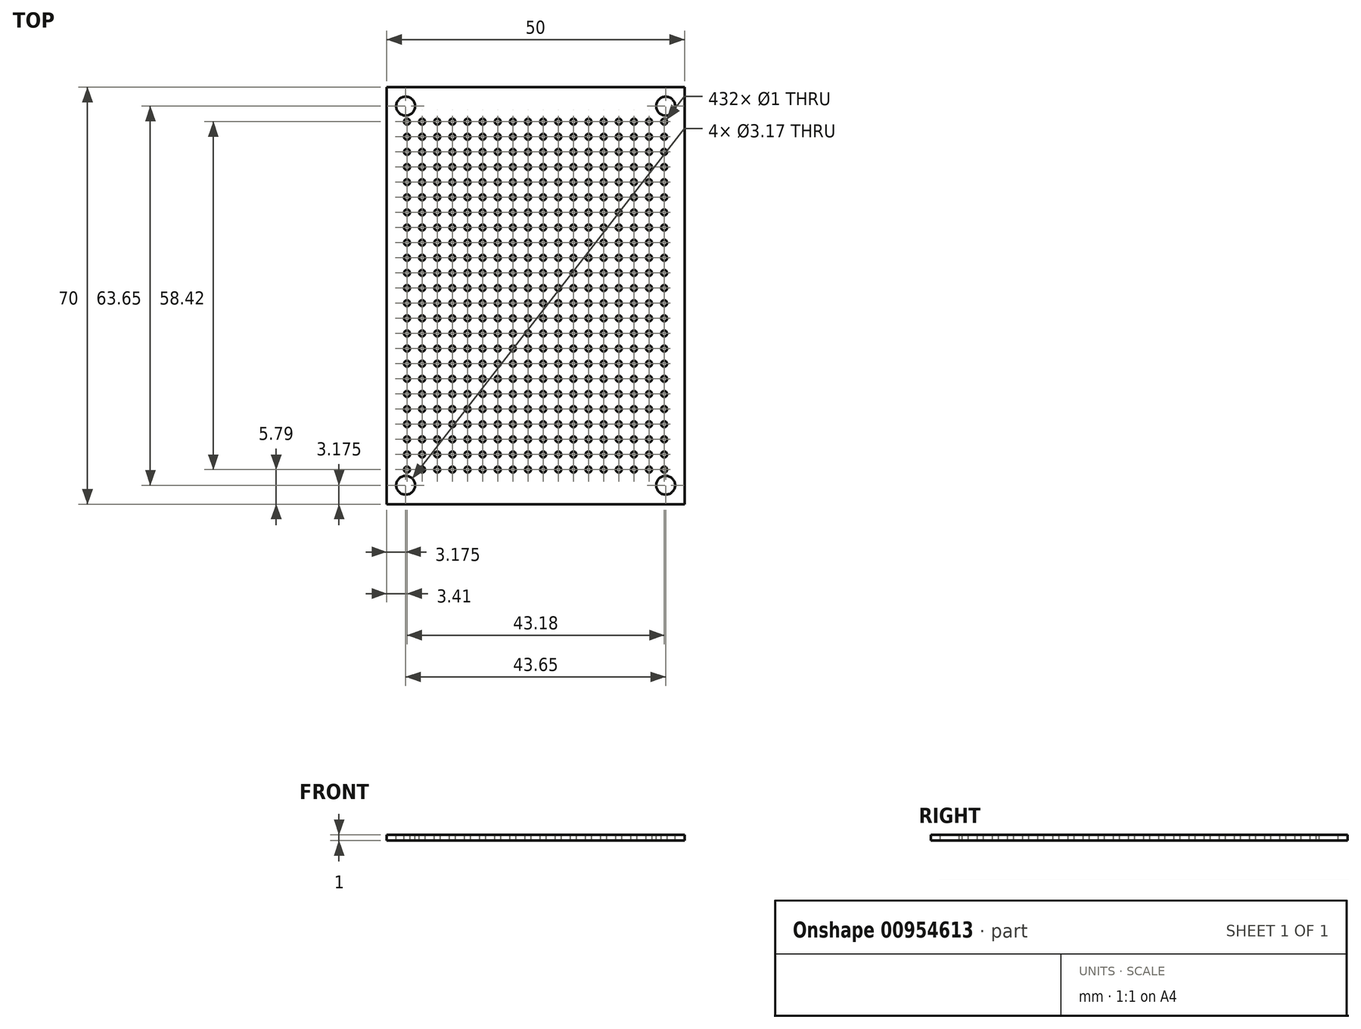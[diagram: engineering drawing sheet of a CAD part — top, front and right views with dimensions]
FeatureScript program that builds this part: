
annotation { "Feature Type Name" : "Feature", "Feature Type Description" : "" }
export const myFeature = defineFeature(function(context is Context, id is Id, definition is map)
    precondition{}
    {
        {
            var Q0;
            Q0=qCreatedBy(makeId("Top.planeOp"),FACE);
            var sketch = newSketch(context, id + "F0", { "sketchPlane" : qUnion([Q0])});
            skLineSegment(sketch, "E0.bottom", {"start": v(-25, 35) * mm, "end": v(25, 35) * mm});
            skLineSegment(sketch, "E0.top", {"start": v(-25, -35) * mm, "end": v(25, -35) * mm});
            skLineSegment(sketch, "E0.left", {"start": v(-25, 35) * mm, "end": v(-25, -35) * mm});
            skLineSegment(sketch, "E0.right", {"start": v(25, 35) * mm, "end": v(25, -35) * mm});
            skPoint(sketch, "E0.middle", {"position": v(0, 0) * mm});
            skSolve(sketch);
        }
        {
            var Q0;
            Q0=qSketchRegion(id+"F0",true);
            extrude(context, id + "F1", {"entities" : qUnion([Q0]), "depth" : 1 * mm, "offsetDistance" : 25 * mm});
        }
        {
            var Q0;
            Q0=makeQuery(id+"F1.opExtrude","CAP_FACE",FACE,{"disambiguationData":[OSD([sQuery(id+"F0.wireOp",EDGE,"E0.bottom"),sQuery(id+"F0.wireOp",EDGE,"E0.top"),sQuery(id+"F0.wireOp",EDGE,"E0.left"),sQuery(id+"F0.wireOp",EDGE,"E0.right")])],"isStart":false});
            var sketch = newSketch(context, id + "F2", { "sketchPlane" : qUnion([Q0])});
            skCircle(sketch, "E1", {"center": v(-21.59, 29.21) * mm, "radius": 0.5 * mm});
            skCircle(sketch, "E2.0.1.0", {"center": v(-21.59, 26.67) * mm, "radius": 0.5 * mm});
            skCircle(sketch, "E2.0.2.0", {"center": v(-21.59, 24.13) * mm, "radius": 0.5 * mm});
            skCircle(sketch, "E2.0.3.0", {"center": v(-21.59, 21.6) * mm, "radius": 0.5 * mm});
            skCircle(sketch, "E2.0.4.0", {"center": v(-21.59, 19.05) * mm, "radius": 0.5 * mm});
            skCircle(sketch, "E2.0.5.0", {"center": v(-21.59, 16.51) * mm, "radius": 0.5 * mm});
            skCircle(sketch, "E2.0.6.0", {"center": v(-21.59, 13.97) * mm, "radius": 0.5 * mm});
            skCircle(sketch, "E2.0.7.0", {"center": v(-21.59, 11.43) * mm, "radius": 0.5 * mm});
            skCircle(sketch, "E2.0.8.0", {"center": v(-21.59, 8.9) * mm, "radius": 0.5 * mm});
            skCircle(sketch, "E2.0.9.0", {"center": v(-21.59, 6.35) * mm, "radius": 0.5 * mm});
            skCircle(sketch, "E2.0.10.0", {"center": v(-21.59, 3.81) * mm, "radius": 0.5 * mm});
            skCircle(sketch, "E2.0.11.0", {"center": v(-21.59, 1.27) * mm, "radius": 0.5 * mm});
            skCircle(sketch, "E2.0.12.0", {"center": v(-21.59, -1.27) * mm, "radius": 0.5 * mm});
            skCircle(sketch, "E2.0.13.0", {"center": v(-21.59, -3.8) * mm, "radius": 0.5 * mm});
            skCircle(sketch, "E2.0.14.0", {"center": v(-21.59, -6.35) * mm, "radius": 0.5 * mm});
            skCircle(sketch, "E2.0.15.0", {"center": v(-21.59, -8.89) * mm, "radius": 0.5 * mm});
            skCircle(sketch, "E2.0.16.0", {"center": v(-21.59, -11.43) * mm, "radius": 0.5 * mm});
            skCircle(sketch, "E2.0.17.0", {"center": v(-21.59, -13.97) * mm, "radius": 0.5 * mm});
            skCircle(sketch, "E2.0.18.0", {"center": v(-21.59, -16.5) * mm, "radius": 0.5 * mm});
            skCircle(sketch, "E2.0.19.0", {"center": v(-21.59, -19.05) * mm, "radius": 0.5 * mm});
            skCircle(sketch, "E2.0.20.0", {"center": v(-21.59, -21.59) * mm, "radius": 0.5 * mm});
            skCircle(sketch, "E2.0.21.0", {"center": v(-21.59, -24.13) * mm, "radius": 0.5 * mm});
            skCircle(sketch, "E2.0.22.0", {"center": v(-21.59, -26.67) * mm, "radius": 0.5 * mm});
            skCircle(sketch, "E2.0.23.0", {"center": v(-21.59, -29.2) * mm, "radius": 0.5 * mm});
            skCircle(sketch, "E2.1.0.0", {"center": v(-19.05, 29.21) * mm, "radius": 0.5 * mm});
            skCircle(sketch, "E2.1.1.0", {"center": v(-19.05, 26.67) * mm, "radius": 0.5 * mm});
            skCircle(sketch, "E2.1.2.0", {"center": v(-19.05, 24.13) * mm, "radius": 0.5 * mm});
            skCircle(sketch, "E2.1.3.0", {"center": v(-19.05, 21.6) * mm, "radius": 0.5 * mm});
            skCircle(sketch, "E2.1.4.0", {"center": v(-19.05, 19.05) * mm, "radius": 0.5 * mm});
            skCircle(sketch, "E2.1.5.0", {"center": v(-19.05, 16.51) * mm, "radius": 0.5 * mm});
            skCircle(sketch, "E2.1.6.0", {"center": v(-19.05, 13.97) * mm, "radius": 0.5 * mm});
            skCircle(sketch, "E2.1.7.0", {"center": v(-19.05, 11.43) * mm, "radius": 0.5 * mm});
            skCircle(sketch, "E2.1.8.0", {"center": v(-19.05, 8.9) * mm, "radius": 0.5 * mm});
            skCircle(sketch, "E2.1.9.0", {"center": v(-19.05, 6.35) * mm, "radius": 0.5 * mm});
            skCircle(sketch, "E2.1.10.0", {"center": v(-19.05, 3.81) * mm, "radius": 0.5 * mm});
            skCircle(sketch, "E2.1.11.0", {"center": v(-19.05, 1.27) * mm, "radius": 0.5 * mm});
            skCircle(sketch, "E2.1.12.0", {"center": v(-19.05, -1.27) * mm, "radius": 0.5 * mm});
            skCircle(sketch, "E2.1.13.0", {"center": v(-19.05, -3.8) * mm, "radius": 0.5 * mm});
            skCircle(sketch, "E2.1.14.0", {"center": v(-19.05, -6.35) * mm, "radius": 0.5 * mm});
            skCircle(sketch, "E2.1.15.0", {"center": v(-19.05, -8.89) * mm, "radius": 0.5 * mm});
            skCircle(sketch, "E2.1.16.0", {"center": v(-19.05, -11.43) * mm, "radius": 0.5 * mm});
            skCircle(sketch, "E2.1.17.0", {"center": v(-19.05, -13.97) * mm, "radius": 0.5 * mm});
            skCircle(sketch, "E2.1.18.0", {"center": v(-19.05, -16.5) * mm, "radius": 0.5 * mm});
            skCircle(sketch, "E2.1.19.0", {"center": v(-19.05, -19.05) * mm, "radius": 0.5 * mm});
            skCircle(sketch, "E2.1.20.0", {"center": v(-19.05, -21.59) * mm, "radius": 0.5 * mm});
            skCircle(sketch, "E2.1.21.0", {"center": v(-19.05, -24.13) * mm, "radius": 0.5 * mm});
            skCircle(sketch, "E2.1.22.0", {"center": v(-19.05, -26.67) * mm, "radius": 0.5 * mm});
            skCircle(sketch, "E2.1.23.0", {"center": v(-19.05, -29.2) * mm, "radius": 0.5 * mm});
            skCircle(sketch, "E2.2.0.0", {"center": v(-16.5, 29.21) * mm, "radius": 0.5 * mm});
            skCircle(sketch, "E2.2.1.0", {"center": v(-16.5, 26.67) * mm, "radius": 0.5 * mm});
            skCircle(sketch, "E2.2.2.0", {"center": v(-16.5, 24.13) * mm, "radius": 0.5 * mm});
            skCircle(sketch, "E2.2.3.0", {"center": v(-16.5, 21.6) * mm, "radius": 0.5 * mm});
            skCircle(sketch, "E2.2.4.0", {"center": v(-16.5, 19.05) * mm, "radius": 0.5 * mm});
            skCircle(sketch, "E2.2.5.0", {"center": v(-16.5, 16.51) * mm, "radius": 0.5 * mm});
            skCircle(sketch, "E2.2.6.0", {"center": v(-16.5, 13.97) * mm, "radius": 0.5 * mm});
            skCircle(sketch, "E2.2.7.0", {"center": v(-16.5, 11.43) * mm, "radius": 0.5 * mm});
            skCircle(sketch, "E2.2.8.0", {"center": v(-16.5, 8.9) * mm, "radius": 0.5 * mm});
            skCircle(sketch, "E2.2.9.0", {"center": v(-16.5, 6.35) * mm, "radius": 0.5 * mm});
            skCircle(sketch, "E2.2.10.0", {"center": v(-16.5, 3.81) * mm, "radius": 0.5 * mm});
            skCircle(sketch, "E2.2.11.0", {"center": v(-16.5, 1.27) * mm, "radius": 0.5 * mm});
            skCircle(sketch, "E2.2.12.0", {"center": v(-16.5, -1.27) * mm, "radius": 0.5 * mm});
            skCircle(sketch, "E2.2.13.0", {"center": v(-16.5, -3.8) * mm, "radius": 0.5 * mm});
            skCircle(sketch, "E2.2.14.0", {"center": v(-16.5, -6.35) * mm, "radius": 0.5 * mm});
            skCircle(sketch, "E2.2.15.0", {"center": v(-16.5, -8.89) * mm, "radius": 0.5 * mm});
            skCircle(sketch, "E2.2.16.0", {"center": v(-16.5, -11.43) * mm, "radius": 0.5 * mm});
            skCircle(sketch, "E2.2.17.0", {"center": v(-16.5, -13.97) * mm, "radius": 0.5 * mm});
            skCircle(sketch, "E2.2.18.0", {"center": v(-16.5, -16.5) * mm, "radius": 0.5 * mm});
            skCircle(sketch, "E2.2.19.0", {"center": v(-16.5, -19.05) * mm, "radius": 0.5 * mm});
            skCircle(sketch, "E2.2.20.0", {"center": v(-16.5, -21.59) * mm, "radius": 0.5 * mm});
            skCircle(sketch, "E2.2.21.0", {"center": v(-16.5, -24.13) * mm, "radius": 0.5 * mm});
            skCircle(sketch, "E2.2.22.0", {"center": v(-16.5, -26.67) * mm, "radius": 0.5 * mm});
            skCircle(sketch, "E2.2.23.0", {"center": v(-16.5, -29.2) * mm, "radius": 0.5 * mm});
            skCircle(sketch, "E2.3.0.0", {"center": v(-13.97, 29.21) * mm, "radius": 0.5 * mm});
            skCircle(sketch, "E2.3.1.0", {"center": v(-13.97, 26.67) * mm, "radius": 0.5 * mm});
            skCircle(sketch, "E2.3.2.0", {"center": v(-13.97, 24.13) * mm, "radius": 0.5 * mm});
            skCircle(sketch, "E2.3.3.0", {"center": v(-13.97, 21.6) * mm, "radius": 0.5 * mm});
            skCircle(sketch, "E2.3.4.0", {"center": v(-13.97, 19.05) * mm, "radius": 0.5 * mm});
            skCircle(sketch, "E2.3.5.0", {"center": v(-13.97, 16.51) * mm, "radius": 0.5 * mm});
            skCircle(sketch, "E2.3.6.0", {"center": v(-13.97, 13.97) * mm, "radius": 0.5 * mm});
            skCircle(sketch, "E2.3.7.0", {"center": v(-13.97, 11.43) * mm, "radius": 0.5 * mm});
            skCircle(sketch, "E2.3.8.0", {"center": v(-13.97, 8.9) * mm, "radius": 0.5 * mm});
            skCircle(sketch, "E2.3.9.0", {"center": v(-13.97, 6.35) * mm, "radius": 0.5 * mm});
            skCircle(sketch, "E2.3.10.0", {"center": v(-13.97, 3.81) * mm, "radius": 0.5 * mm});
            skCircle(sketch, "E2.3.11.0", {"center": v(-13.97, 1.27) * mm, "radius": 0.5 * mm});
            skCircle(sketch, "E2.3.12.0", {"center": v(-13.97, -1.27) * mm, "radius": 0.5 * mm});
            skCircle(sketch, "E2.3.13.0", {"center": v(-13.97, -3.8) * mm, "radius": 0.5 * mm});
            skCircle(sketch, "E2.3.14.0", {"center": v(-13.97, -6.35) * mm, "radius": 0.5 * mm});
            skCircle(sketch, "E2.3.15.0", {"center": v(-13.97, -8.89) * mm, "radius": 0.5 * mm});
            skCircle(sketch, "E2.3.16.0", {"center": v(-13.97, -11.43) * mm, "radius": 0.5 * mm});
            skCircle(sketch, "E2.3.17.0", {"center": v(-13.97, -13.97) * mm, "radius": 0.5 * mm});
            skCircle(sketch, "E2.3.18.0", {"center": v(-13.97, -16.5) * mm, "radius": 0.5 * mm});
            skCircle(sketch, "E2.3.19.0", {"center": v(-13.97, -19.05) * mm, "radius": 0.5 * mm});
            skCircle(sketch, "E2.3.20.0", {"center": v(-13.97, -21.59) * mm, "radius": 0.5 * mm});
            skCircle(sketch, "E2.3.21.0", {"center": v(-13.97, -24.13) * mm, "radius": 0.5 * mm});
            skCircle(sketch, "E2.3.22.0", {"center": v(-13.97, -26.67) * mm, "radius": 0.5 * mm});
            skCircle(sketch, "E2.3.23.0", {"center": v(-13.97, -29.2) * mm, "radius": 0.5 * mm});
            skCircle(sketch, "E2.4.0.0", {"center": v(-11.43, 29.21) * mm, "radius": 0.5 * mm});
            skCircle(sketch, "E2.4.1.0", {"center": v(-11.43, 26.67) * mm, "radius": 0.5 * mm});
            skCircle(sketch, "E2.4.2.0", {"center": v(-11.43, 24.13) * mm, "radius": 0.5 * mm});
            skCircle(sketch, "E2.4.3.0", {"center": v(-11.43, 21.6) * mm, "radius": 0.5 * mm});
            skCircle(sketch, "E2.4.4.0", {"center": v(-11.43, 19.05) * mm, "radius": 0.5 * mm});
            skCircle(sketch, "E2.4.5.0", {"center": v(-11.43, 16.51) * mm, "radius": 0.5 * mm});
            skCircle(sketch, "E2.4.6.0", {"center": v(-11.43, 13.97) * mm, "radius": 0.5 * mm});
            skCircle(sketch, "E2.4.7.0", {"center": v(-11.43, 11.43) * mm, "radius": 0.5 * mm});
            skCircle(sketch, "E2.4.8.0", {"center": v(-11.43, 8.9) * mm, "radius": 0.5 * mm});
            skCircle(sketch, "E2.4.9.0", {"center": v(-11.43, 6.35) * mm, "radius": 0.5 * mm});
            skCircle(sketch, "E2.4.10.0", {"center": v(-11.43, 3.81) * mm, "radius": 0.5 * mm});
            skCircle(sketch, "E2.4.11.0", {"center": v(-11.43, 1.27) * mm, "radius": 0.5 * mm});
            skCircle(sketch, "E2.4.12.0", {"center": v(-11.43, -1.27) * mm, "radius": 0.5 * mm});
            skCircle(sketch, "E2.4.13.0", {"center": v(-11.43, -3.8) * mm, "radius": 0.5 * mm});
            skCircle(sketch, "E2.4.14.0", {"center": v(-11.43, -6.35) * mm, "radius": 0.5 * mm});
            skCircle(sketch, "E2.4.15.0", {"center": v(-11.43, -8.89) * mm, "radius": 0.5 * mm});
            skCircle(sketch, "E2.4.16.0", {"center": v(-11.43, -11.43) * mm, "radius": 0.5 * mm});
            skCircle(sketch, "E2.4.17.0", {"center": v(-11.43, -13.97) * mm, "radius": 0.5 * mm});
            skCircle(sketch, "E2.4.18.0", {"center": v(-11.43, -16.5) * mm, "radius": 0.5 * mm});
            skCircle(sketch, "E2.4.19.0", {"center": v(-11.43, -19.05) * mm, "radius": 0.5 * mm});
            skCircle(sketch, "E2.4.20.0", {"center": v(-11.43, -21.59) * mm, "radius": 0.5 * mm});
            skCircle(sketch, "E2.4.21.0", {"center": v(-11.43, -24.13) * mm, "radius": 0.5 * mm});
            skCircle(sketch, "E2.4.22.0", {"center": v(-11.43, -26.67) * mm, "radius": 0.5 * mm});
            skCircle(sketch, "E2.4.23.0", {"center": v(-11.43, -29.2) * mm, "radius": 0.5 * mm});
            skCircle(sketch, "E2.5.0.0", {"center": v(-8.89, 29.21) * mm, "radius": 0.5 * mm});
            skCircle(sketch, "E2.5.1.0", {"center": v(-8.89, 26.67) * mm, "radius": 0.5 * mm});
            skCircle(sketch, "E2.5.2.0", {"center": v(-8.89, 24.13) * mm, "radius": 0.5 * mm});
            skCircle(sketch, "E2.5.3.0", {"center": v(-8.89, 21.6) * mm, "radius": 0.5 * mm});
            skCircle(sketch, "E2.5.4.0", {"center": v(-8.89, 19.05) * mm, "radius": 0.5 * mm});
            skCircle(sketch, "E2.5.5.0", {"center": v(-8.89, 16.51) * mm, "radius": 0.5 * mm});
            skCircle(sketch, "E2.5.6.0", {"center": v(-8.89, 13.97) * mm, "radius": 0.5 * mm});
            skCircle(sketch, "E2.5.7.0", {"center": v(-8.89, 11.43) * mm, "radius": 0.5 * mm});
            skCircle(sketch, "E2.5.8.0", {"center": v(-8.89, 8.9) * mm, "radius": 0.5 * mm});
            skCircle(sketch, "E2.5.9.0", {"center": v(-8.89, 6.35) * mm, "radius": 0.5 * mm});
            skCircle(sketch, "E2.5.10.0", {"center": v(-8.89, 3.81) * mm, "radius": 0.5 * mm});
            skCircle(sketch, "E2.5.11.0", {"center": v(-8.89, 1.27) * mm, "radius": 0.5 * mm});
            skCircle(sketch, "E2.5.12.0", {"center": v(-8.89, -1.27) * mm, "radius": 0.5 * mm});
            skCircle(sketch, "E2.5.13.0", {"center": v(-8.89, -3.8) * mm, "radius": 0.5 * mm});
            skCircle(sketch, "E2.5.14.0", {"center": v(-8.89, -6.35) * mm, "radius": 0.5 * mm});
            skCircle(sketch, "E2.5.15.0", {"center": v(-8.89, -8.89) * mm, "radius": 0.5 * mm});
            skCircle(sketch, "E2.5.16.0", {"center": v(-8.89, -11.43) * mm, "radius": 0.5 * mm});
            skCircle(sketch, "E2.5.17.0", {"center": v(-8.89, -13.97) * mm, "radius": 0.5 * mm});
            skCircle(sketch, "E2.5.18.0", {"center": v(-8.89, -16.5) * mm, "radius": 0.5 * mm});
            skCircle(sketch, "E2.5.19.0", {"center": v(-8.89, -19.05) * mm, "radius": 0.5 * mm});
            skCircle(sketch, "E2.5.20.0", {"center": v(-8.89, -21.59) * mm, "radius": 0.5 * mm});
            skCircle(sketch, "E2.5.21.0", {"center": v(-8.89, -24.13) * mm, "radius": 0.5 * mm});
            skCircle(sketch, "E2.5.22.0", {"center": v(-8.89, -26.67) * mm, "radius": 0.5 * mm});
            skCircle(sketch, "E2.5.23.0", {"center": v(-8.89, -29.2) * mm, "radius": 0.5 * mm});
            skCircle(sketch, "E2.6.0.0", {"center": v(-6.35, 29.21) * mm, "radius": 0.5 * mm});
            skCircle(sketch, "E2.6.1.0", {"center": v(-6.35, 26.67) * mm, "radius": 0.5 * mm});
            skCircle(sketch, "E2.6.2.0", {"center": v(-6.35, 24.13) * mm, "radius": 0.5 * mm});
            skCircle(sketch, "E2.6.3.0", {"center": v(-6.35, 21.6) * mm, "radius": 0.5 * mm});
            skCircle(sketch, "E2.6.4.0", {"center": v(-6.35, 19.05) * mm, "radius": 0.5 * mm});
            skCircle(sketch, "E2.6.5.0", {"center": v(-6.35, 16.51) * mm, "radius": 0.5 * mm});
            skCircle(sketch, "E2.6.6.0", {"center": v(-6.35, 13.97) * mm, "radius": 0.5 * mm});
            skCircle(sketch, "E2.6.7.0", {"center": v(-6.35, 11.43) * mm, "radius": 0.5 * mm});
            skCircle(sketch, "E2.6.8.0", {"center": v(-6.35, 8.9) * mm, "radius": 0.5 * mm});
            skCircle(sketch, "E2.6.9.0", {"center": v(-6.35, 6.35) * mm, "radius": 0.5 * mm});
            skCircle(sketch, "E2.6.10.0", {"center": v(-6.35, 3.81) * mm, "radius": 0.5 * mm});
            skCircle(sketch, "E2.6.11.0", {"center": v(-6.35, 1.27) * mm, "radius": 0.5 * mm});
            skCircle(sketch, "E2.6.12.0", {"center": v(-6.35, -1.27) * mm, "radius": 0.5 * mm});
            skCircle(sketch, "E2.6.13.0", {"center": v(-6.35, -3.8) * mm, "radius": 0.5 * mm});
            skCircle(sketch, "E2.6.14.0", {"center": v(-6.35, -6.35) * mm, "radius": 0.5 * mm});
            skCircle(sketch, "E2.6.15.0", {"center": v(-6.35, -8.89) * mm, "radius": 0.5 * mm});
            skCircle(sketch, "E2.6.16.0", {"center": v(-6.35, -11.43) * mm, "radius": 0.5 * mm});
            skCircle(sketch, "E2.6.17.0", {"center": v(-6.35, -13.97) * mm, "radius": 0.5 * mm});
            skCircle(sketch, "E2.6.18.0", {"center": v(-6.35, -16.5) * mm, "radius": 0.5 * mm});
            skCircle(sketch, "E2.6.19.0", {"center": v(-6.35, -19.05) * mm, "radius": 0.5 * mm});
            skCircle(sketch, "E2.6.20.0", {"center": v(-6.35, -21.59) * mm, "radius": 0.5 * mm});
            skCircle(sketch, "E2.6.21.0", {"center": v(-6.35, -24.13) * mm, "radius": 0.5 * mm});
            skCircle(sketch, "E2.6.22.0", {"center": v(-6.35, -26.67) * mm, "radius": 0.5 * mm});
            skCircle(sketch, "E2.6.23.0", {"center": v(-6.35, -29.2) * mm, "radius": 0.5 * mm});
            skCircle(sketch, "E2.7.0.0", {"center": v(-3.8, 29.21) * mm, "radius": 0.5 * mm});
            skCircle(sketch, "E2.7.1.0", {"center": v(-3.8, 26.67) * mm, "radius": 0.5 * mm});
            skCircle(sketch, "E2.7.2.0", {"center": v(-3.8, 24.13) * mm, "radius": 0.5 * mm});
            skCircle(sketch, "E2.7.3.0", {"center": v(-3.8, 21.6) * mm, "radius": 0.5 * mm});
            skCircle(sketch, "E2.7.4.0", {"center": v(-3.8, 19.05) * mm, "radius": 0.5 * mm});
            skCircle(sketch, "E2.7.5.0", {"center": v(-3.8, 16.51) * mm, "radius": 0.5 * mm});
            skCircle(sketch, "E2.7.6.0", {"center": v(-3.8, 13.97) * mm, "radius": 0.5 * mm});
            skCircle(sketch, "E2.7.7.0", {"center": v(-3.8, 11.43) * mm, "radius": 0.5 * mm});
            skCircle(sketch, "E2.7.8.0", {"center": v(-3.8, 8.9) * mm, "radius": 0.5 * mm});
            skCircle(sketch, "E2.7.9.0", {"center": v(-3.8, 6.35) * mm, "radius": 0.5 * mm});
            skCircle(sketch, "E2.7.10.0", {"center": v(-3.8, 3.81) * mm, "radius": 0.5 * mm});
            skCircle(sketch, "E2.7.11.0", {"center": v(-3.8, 1.27) * mm, "radius": 0.5 * mm});
            skCircle(sketch, "E2.7.12.0", {"center": v(-3.8, -1.27) * mm, "radius": 0.5 * mm});
            skCircle(sketch, "E2.7.13.0", {"center": v(-3.8, -3.8) * mm, "radius": 0.5 * mm});
            skCircle(sketch, "E2.7.14.0", {"center": v(-3.8, -6.35) * mm, "radius": 0.5 * mm});
            skCircle(sketch, "E2.7.15.0", {"center": v(-3.8, -8.89) * mm, "radius": 0.5 * mm});
            skCircle(sketch, "E2.7.16.0", {"center": v(-3.8, -11.43) * mm, "radius": 0.5 * mm});
            skCircle(sketch, "E2.7.17.0", {"center": v(-3.8, -13.97) * mm, "radius": 0.5 * mm});
            skCircle(sketch, "E2.7.18.0", {"center": v(-3.8, -16.5) * mm, "radius": 0.5 * mm});
            skCircle(sketch, "E2.7.19.0", {"center": v(-3.8, -19.05) * mm, "radius": 0.5 * mm});
            skCircle(sketch, "E2.7.20.0", {"center": v(-3.8, -21.59) * mm, "radius": 0.5 * mm});
            skCircle(sketch, "E2.7.21.0", {"center": v(-3.8, -24.13) * mm, "radius": 0.5 * mm});
            skCircle(sketch, "E2.7.22.0", {"center": v(-3.8, -26.67) * mm, "radius": 0.5 * mm});
            skCircle(sketch, "E2.7.23.0", {"center": v(-3.8, -29.2) * mm, "radius": 0.5 * mm});
            skCircle(sketch, "E2.8.0.0", {"center": v(-1.27, 29.21) * mm, "radius": 0.5 * mm});
            skCircle(sketch, "E2.8.1.0", {"center": v(-1.27, 26.67) * mm, "radius": 0.5 * mm});
            skCircle(sketch, "E2.8.2.0", {"center": v(-1.27, 24.13) * mm, "radius": 0.5 * mm});
            skCircle(sketch, "E2.8.3.0", {"center": v(-1.27, 21.6) * mm, "radius": 0.5 * mm});
            skCircle(sketch, "E2.8.4.0", {"center": v(-1.27, 19.05) * mm, "radius": 0.5 * mm});
            skCircle(sketch, "E2.8.5.0", {"center": v(-1.27, 16.51) * mm, "radius": 0.5 * mm});
            skCircle(sketch, "E2.8.6.0", {"center": v(-1.27, 13.97) * mm, "radius": 0.5 * mm});
            skCircle(sketch, "E2.8.7.0", {"center": v(-1.27, 11.43) * mm, "radius": 0.5 * mm});
            skCircle(sketch, "E2.8.8.0", {"center": v(-1.27, 8.9) * mm, "radius": 0.5 * mm});
            skCircle(sketch, "E2.8.9.0", {"center": v(-1.27, 6.35) * mm, "radius": 0.5 * mm});
            skCircle(sketch, "E2.8.10.0", {"center": v(-1.27, 3.81) * mm, "radius": 0.5 * mm});
            skCircle(sketch, "E2.8.11.0", {"center": v(-1.27, 1.27) * mm, "radius": 0.5 * mm});
            skCircle(sketch, "E2.8.12.0", {"center": v(-1.27, -1.27) * mm, "radius": 0.5 * mm});
            skCircle(sketch, "E2.8.13.0", {"center": v(-1.27, -3.8) * mm, "radius": 0.5 * mm});
            skCircle(sketch, "E2.8.14.0", {"center": v(-1.27, -6.35) * mm, "radius": 0.5 * mm});
            skCircle(sketch, "E2.8.15.0", {"center": v(-1.27, -8.89) * mm, "radius": 0.5 * mm});
            skCircle(sketch, "E2.8.16.0", {"center": v(-1.27, -11.43) * mm, "radius": 0.5 * mm});
            skCircle(sketch, "E2.8.17.0", {"center": v(-1.27, -13.97) * mm, "radius": 0.5 * mm});
            skCircle(sketch, "E2.8.18.0", {"center": v(-1.27, -16.5) * mm, "radius": 0.5 * mm});
            skCircle(sketch, "E2.8.19.0", {"center": v(-1.27, -19.05) * mm, "radius": 0.5 * mm});
            skCircle(sketch, "E2.8.20.0", {"center": v(-1.27, -21.59) * mm, "radius": 0.5 * mm});
            skCircle(sketch, "E2.8.21.0", {"center": v(-1.27, -24.13) * mm, "radius": 0.5 * mm});
            skCircle(sketch, "E2.8.22.0", {"center": v(-1.27, -26.67) * mm, "radius": 0.5 * mm});
            skCircle(sketch, "E2.8.23.0", {"center": v(-1.27, -29.2) * mm, "radius": 0.5 * mm});
            skCircle(sketch, "E2.9.0.0", {"center": v(1.27, 29.21) * mm, "radius": 0.5 * mm});
            skCircle(sketch, "E2.9.1.0", {"center": v(1.27, 26.67) * mm, "radius": 0.5 * mm});
            skCircle(sketch, "E2.9.2.0", {"center": v(1.27, 24.13) * mm, "radius": 0.5 * mm});
            skCircle(sketch, "E2.9.3.0", {"center": v(1.27, 21.6) * mm, "radius": 0.5 * mm});
            skCircle(sketch, "E2.9.4.0", {"center": v(1.27, 19.05) * mm, "radius": 0.5 * mm});
            skCircle(sketch, "E2.9.5.0", {"center": v(1.27, 16.51) * mm, "radius": 0.5 * mm});
            skCircle(sketch, "E2.9.6.0", {"center": v(1.27, 13.97) * mm, "radius": 0.5 * mm});
            skCircle(sketch, "E2.9.7.0", {"center": v(1.27, 11.43) * mm, "radius": 0.5 * mm});
            skCircle(sketch, "E2.9.8.0", {"center": v(1.27, 8.9) * mm, "radius": 0.5 * mm});
            skCircle(sketch, "E2.9.9.0", {"center": v(1.27, 6.35) * mm, "radius": 0.5 * mm});
            skCircle(sketch, "E2.9.10.0", {"center": v(1.27, 3.81) * mm, "radius": 0.5 * mm});
            skCircle(sketch, "E2.9.11.0", {"center": v(1.27, 1.27) * mm, "radius": 0.5 * mm});
            skCircle(sketch, "E2.9.12.0", {"center": v(1.27, -1.27) * mm, "radius": 0.5 * mm});
            skCircle(sketch, "E2.9.13.0", {"center": v(1.27, -3.8) * mm, "radius": 0.5 * mm});
            skCircle(sketch, "E2.9.14.0", {"center": v(1.27, -6.35) * mm, "radius": 0.5 * mm});
            skCircle(sketch, "E2.9.15.0", {"center": v(1.27, -8.89) * mm, "radius": 0.5 * mm});
            skCircle(sketch, "E2.9.16.0", {"center": v(1.27, -11.43) * mm, "radius": 0.5 * mm});
            skCircle(sketch, "E2.9.17.0", {"center": v(1.27, -13.97) * mm, "radius": 0.5 * mm});
            skCircle(sketch, "E2.9.18.0", {"center": v(1.27, -16.5) * mm, "radius": 0.5 * mm});
            skCircle(sketch, "E2.9.19.0", {"center": v(1.27, -19.05) * mm, "radius": 0.5 * mm});
            skCircle(sketch, "E2.9.20.0", {"center": v(1.27, -21.59) * mm, "radius": 0.5 * mm});
            skCircle(sketch, "E2.9.21.0", {"center": v(1.27, -24.13) * mm, "radius": 0.5 * mm});
            skCircle(sketch, "E2.9.22.0", {"center": v(1.27, -26.67) * mm, "radius": 0.5 * mm});
            skCircle(sketch, "E2.9.23.0", {"center": v(1.27, -29.2) * mm, "radius": 0.5 * mm});
            skCircle(sketch, "E2.10.0.0", {"center": v(3.81, 29.21) * mm, "radius": 0.5 * mm});
            skCircle(sketch, "E2.10.1.0", {"center": v(3.81, 26.67) * mm, "radius": 0.5 * mm});
            skCircle(sketch, "E2.10.2.0", {"center": v(3.81, 24.13) * mm, "radius": 0.5 * mm});
            skCircle(sketch, "E2.10.3.0", {"center": v(3.81, 21.6) * mm, "radius": 0.5 * mm});
            skCircle(sketch, "E2.10.4.0", {"center": v(3.81, 19.05) * mm, "radius": 0.5 * mm});
            skCircle(sketch, "E2.10.5.0", {"center": v(3.81, 16.51) * mm, "radius": 0.5 * mm});
            skCircle(sketch, "E2.10.6.0", {"center": v(3.81, 13.97) * mm, "radius": 0.5 * mm});
            skCircle(sketch, "E2.10.7.0", {"center": v(3.81, 11.43) * mm, "radius": 0.5 * mm});
            skCircle(sketch, "E2.10.8.0", {"center": v(3.81, 8.9) * mm, "radius": 0.5 * mm});
            skCircle(sketch, "E2.10.9.0", {"center": v(3.81, 6.35) * mm, "radius": 0.5 * mm});
            skCircle(sketch, "E2.10.10.0", {"center": v(3.81, 3.81) * mm, "radius": 0.5 * mm});
            skCircle(sketch, "E2.10.11.0", {"center": v(3.81, 1.27) * mm, "radius": 0.5 * mm});
            skCircle(sketch, "E2.10.12.0", {"center": v(3.81, -1.27) * mm, "radius": 0.5 * mm});
            skCircle(sketch, "E2.10.13.0", {"center": v(3.81, -3.8) * mm, "radius": 0.5 * mm});
            skCircle(sketch, "E2.10.14.0", {"center": v(3.81, -6.35) * mm, "radius": 0.5 * mm});
            skCircle(sketch, "E2.10.15.0", {"center": v(3.81, -8.89) * mm, "radius": 0.5 * mm});
            skCircle(sketch, "E2.10.16.0", {"center": v(3.81, -11.43) * mm, "radius": 0.5 * mm});
            skCircle(sketch, "E2.10.17.0", {"center": v(3.81, -13.97) * mm, "radius": 0.5 * mm});
            skCircle(sketch, "E2.10.18.0", {"center": v(3.81, -16.5) * mm, "radius": 0.5 * mm});
            skCircle(sketch, "E2.10.19.0", {"center": v(3.81, -19.05) * mm, "radius": 0.5 * mm});
            skCircle(sketch, "E2.10.20.0", {"center": v(3.81, -21.59) * mm, "radius": 0.5 * mm});
            skCircle(sketch, "E2.10.21.0", {"center": v(3.81, -24.13) * mm, "radius": 0.5 * mm});
            skCircle(sketch, "E2.10.22.0", {"center": v(3.81, -26.67) * mm, "radius": 0.5 * mm});
            skCircle(sketch, "E2.10.23.0", {"center": v(3.81, -29.2) * mm, "radius": 0.5 * mm});
            skCircle(sketch, "E2.11.0.0", {"center": v(6.35, 29.21) * mm, "radius": 0.5 * mm});
            skCircle(sketch, "E2.11.1.0", {"center": v(6.35, 26.67) * mm, "radius": 0.5 * mm});
            skCircle(sketch, "E2.11.2.0", {"center": v(6.35, 24.13) * mm, "radius": 0.5 * mm});
            skCircle(sketch, "E2.11.3.0", {"center": v(6.35, 21.6) * mm, "radius": 0.5 * mm});
            skCircle(sketch, "E2.11.4.0", {"center": v(6.35, 19.05) * mm, "radius": 0.5 * mm});
            skCircle(sketch, "E2.11.5.0", {"center": v(6.35, 16.51) * mm, "radius": 0.5 * mm});
            skCircle(sketch, "E2.11.6.0", {"center": v(6.35, 13.97) * mm, "radius": 0.5 * mm});
            skCircle(sketch, "E2.11.7.0", {"center": v(6.35, 11.43) * mm, "radius": 0.5 * mm});
            skCircle(sketch, "E2.11.8.0", {"center": v(6.35, 8.9) * mm, "radius": 0.5 * mm});
            skCircle(sketch, "E2.11.9.0", {"center": v(6.35, 6.35) * mm, "radius": 0.5 * mm});
            skCircle(sketch, "E2.11.10.0", {"center": v(6.35, 3.81) * mm, "radius": 0.5 * mm});
            skCircle(sketch, "E2.11.11.0", {"center": v(6.35, 1.27) * mm, "radius": 0.5 * mm});
            skCircle(sketch, "E2.11.12.0", {"center": v(6.35, -1.27) * mm, "radius": 0.5 * mm});
            skCircle(sketch, "E2.11.13.0", {"center": v(6.35, -3.8) * mm, "radius": 0.5 * mm});
            skCircle(sketch, "E2.11.14.0", {"center": v(6.35, -6.35) * mm, "radius": 0.5 * mm});
            skCircle(sketch, "E2.11.15.0", {"center": v(6.35, -8.89) * mm, "radius": 0.5 * mm});
            skCircle(sketch, "E2.11.16.0", {"center": v(6.35, -11.43) * mm, "radius": 0.5 * mm});
            skCircle(sketch, "E2.11.17.0", {"center": v(6.35, -13.97) * mm, "radius": 0.5 * mm});
            skCircle(sketch, "E2.11.18.0", {"center": v(6.35, -16.5) * mm, "radius": 0.5 * mm});
            skCircle(sketch, "E2.11.19.0", {"center": v(6.35, -19.05) * mm, "radius": 0.5 * mm});
            skCircle(sketch, "E2.11.20.0", {"center": v(6.35, -21.59) * mm, "radius": 0.5 * mm});
            skCircle(sketch, "E2.11.21.0", {"center": v(6.35, -24.13) * mm, "radius": 0.5 * mm});
            skCircle(sketch, "E2.11.22.0", {"center": v(6.35, -26.67) * mm, "radius": 0.5 * mm});
            skCircle(sketch, "E2.11.23.0", {"center": v(6.35, -29.2) * mm, "radius": 0.5 * mm});
            skCircle(sketch, "E2.12.0.0", {"center": v(8.9, 29.21) * mm, "radius": 0.5 * mm});
            skCircle(sketch, "E2.12.1.0", {"center": v(8.9, 26.67) * mm, "radius": 0.5 * mm});
            skCircle(sketch, "E2.12.2.0", {"center": v(8.9, 24.13) * mm, "radius": 0.5 * mm});
            skCircle(sketch, "E2.12.3.0", {"center": v(8.9, 21.6) * mm, "radius": 0.5 * mm});
            skCircle(sketch, "E2.12.4.0", {"center": v(8.9, 19.05) * mm, "radius": 0.5 * mm});
            skCircle(sketch, "E2.12.5.0", {"center": v(8.9, 16.51) * mm, "radius": 0.5 * mm});
            skCircle(sketch, "E2.12.6.0", {"center": v(8.9, 13.97) * mm, "radius": 0.5 * mm});
            skCircle(sketch, "E2.12.7.0", {"center": v(8.9, 11.43) * mm, "radius": 0.5 * mm});
            skCircle(sketch, "E2.12.8.0", {"center": v(8.9, 8.9) * mm, "radius": 0.5 * mm});
            skCircle(sketch, "E2.12.9.0", {"center": v(8.9, 6.35) * mm, "radius": 0.5 * mm});
            skCircle(sketch, "E2.12.10.0", {"center": v(8.9, 3.81) * mm, "radius": 0.5 * mm});
            skCircle(sketch, "E2.12.11.0", {"center": v(8.9, 1.27) * mm, "radius": 0.5 * mm});
            skCircle(sketch, "E2.12.12.0", {"center": v(8.9, -1.27) * mm, "radius": 0.5 * mm});
            skCircle(sketch, "E2.12.13.0", {"center": v(8.9, -3.8) * mm, "radius": 0.5 * mm});
            skCircle(sketch, "E2.12.14.0", {"center": v(8.9, -6.35) * mm, "radius": 0.5 * mm});
            skCircle(sketch, "E2.12.15.0", {"center": v(8.9, -8.89) * mm, "radius": 0.5 * mm});
            skCircle(sketch, "E2.12.16.0", {"center": v(8.9, -11.43) * mm, "radius": 0.5 * mm});
            skCircle(sketch, "E2.12.17.0", {"center": v(8.9, -13.97) * mm, "radius": 0.5 * mm});
            skCircle(sketch, "E2.12.18.0", {"center": v(8.9, -16.5) * mm, "radius": 0.5 * mm});
            skCircle(sketch, "E2.12.19.0", {"center": v(8.9, -19.05) * mm, "radius": 0.5 * mm});
            skCircle(sketch, "E2.12.20.0", {"center": v(8.9, -21.59) * mm, "radius": 0.5 * mm});
            skCircle(sketch, "E2.12.21.0", {"center": v(8.9, -24.13) * mm, "radius": 0.5 * mm});
            skCircle(sketch, "E2.12.22.0", {"center": v(8.9, -26.67) * mm, "radius": 0.5 * mm});
            skCircle(sketch, "E2.12.23.0", {"center": v(8.9, -29.2) * mm, "radius": 0.5 * mm});
            skCircle(sketch, "E2.13.0.0", {"center": v(11.43, 29.21) * mm, "radius": 0.5 * mm});
            skCircle(sketch, "E2.13.1.0", {"center": v(11.43, 26.67) * mm, "radius": 0.5 * mm});
            skCircle(sketch, "E2.13.2.0", {"center": v(11.43, 24.13) * mm, "radius": 0.5 * mm});
            skCircle(sketch, "E2.13.3.0", {"center": v(11.43, 21.6) * mm, "radius": 0.5 * mm});
            skCircle(sketch, "E2.13.4.0", {"center": v(11.43, 19.05) * mm, "radius": 0.5 * mm});
            skCircle(sketch, "E2.13.5.0", {"center": v(11.43, 16.51) * mm, "radius": 0.5 * mm});
            skCircle(sketch, "E2.13.6.0", {"center": v(11.43, 13.97) * mm, "radius": 0.5 * mm});
            skCircle(sketch, "E2.13.7.0", {"center": v(11.43, 11.43) * mm, "radius": 0.5 * mm});
            skCircle(sketch, "E2.13.8.0", {"center": v(11.43, 8.9) * mm, "radius": 0.5 * mm});
            skCircle(sketch, "E2.13.9.0", {"center": v(11.43, 6.35) * mm, "radius": 0.5 * mm});
            skCircle(sketch, "E2.13.10.0", {"center": v(11.43, 3.81) * mm, "radius": 0.5 * mm});
            skCircle(sketch, "E2.13.11.0", {"center": v(11.43, 1.27) * mm, "radius": 0.5 * mm});
            skCircle(sketch, "E2.13.12.0", {"center": v(11.43, -1.27) * mm, "radius": 0.5 * mm});
            skCircle(sketch, "E2.13.13.0", {"center": v(11.43, -3.8) * mm, "radius": 0.5 * mm});
            skCircle(sketch, "E2.13.14.0", {"center": v(11.43, -6.35) * mm, "radius": 0.5 * mm});
            skCircle(sketch, "E2.13.15.0", {"center": v(11.43, -8.89) * mm, "radius": 0.5 * mm});
            skCircle(sketch, "E2.13.16.0", {"center": v(11.43, -11.43) * mm, "radius": 0.5 * mm});
            skCircle(sketch, "E2.13.17.0", {"center": v(11.43, -13.97) * mm, "radius": 0.5 * mm});
            skCircle(sketch, "E2.13.18.0", {"center": v(11.43, -16.5) * mm, "radius": 0.5 * mm});
            skCircle(sketch, "E2.13.19.0", {"center": v(11.43, -19.05) * mm, "radius": 0.5 * mm});
            skCircle(sketch, "E2.13.20.0", {"center": v(11.43, -21.59) * mm, "radius": 0.5 * mm});
            skCircle(sketch, "E2.13.21.0", {"center": v(11.43, -24.13) * mm, "radius": 0.5 * mm});
            skCircle(sketch, "E2.13.22.0", {"center": v(11.43, -26.67) * mm, "radius": 0.5 * mm});
            skCircle(sketch, "E2.13.23.0", {"center": v(11.43, -29.2) * mm, "radius": 0.5 * mm});
            skCircle(sketch, "E2.14.0.0", {"center": v(13.97, 29.21) * mm, "radius": 0.5 * mm});
            skCircle(sketch, "E2.14.1.0", {"center": v(13.97, 26.67) * mm, "radius": 0.5 * mm});
            skCircle(sketch, "E2.14.2.0", {"center": v(13.97, 24.13) * mm, "radius": 0.5 * mm});
            skCircle(sketch, "E2.14.3.0", {"center": v(13.97, 21.6) * mm, "radius": 0.5 * mm});
            skCircle(sketch, "E2.14.4.0", {"center": v(13.97, 19.05) * mm, "radius": 0.5 * mm});
            skCircle(sketch, "E2.14.5.0", {"center": v(13.97, 16.51) * mm, "radius": 0.5 * mm});
            skCircle(sketch, "E2.14.6.0", {"center": v(13.97, 13.97) * mm, "radius": 0.5 * mm});
            skCircle(sketch, "E2.14.7.0", {"center": v(13.97, 11.43) * mm, "radius": 0.5 * mm});
            skCircle(sketch, "E2.14.8.0", {"center": v(13.97, 8.9) * mm, "radius": 0.5 * mm});
            skCircle(sketch, "E2.14.9.0", {"center": v(13.97, 6.35) * mm, "radius": 0.5 * mm});
            skCircle(sketch, "E2.14.10.0", {"center": v(13.97, 3.81) * mm, "radius": 0.5 * mm});
            skCircle(sketch, "E2.14.11.0", {"center": v(13.97, 1.27) * mm, "radius": 0.5 * mm});
            skCircle(sketch, "E2.14.12.0", {"center": v(13.97, -1.27) * mm, "radius": 0.5 * mm});
            skCircle(sketch, "E2.14.13.0", {"center": v(13.97, -3.8) * mm, "radius": 0.5 * mm});
            skCircle(sketch, "E2.14.14.0", {"center": v(13.97, -6.35) * mm, "radius": 0.5 * mm});
            skCircle(sketch, "E2.14.15.0", {"center": v(13.97, -8.89) * mm, "radius": 0.5 * mm});
            skCircle(sketch, "E2.14.16.0", {"center": v(13.97, -11.43) * mm, "radius": 0.5 * mm});
            skCircle(sketch, "E2.14.17.0", {"center": v(13.97, -13.97) * mm, "radius": 0.5 * mm});
            skCircle(sketch, "E2.14.18.0", {"center": v(13.97, -16.5) * mm, "radius": 0.5 * mm});
            skCircle(sketch, "E2.14.19.0", {"center": v(13.97, -19.05) * mm, "radius": 0.5 * mm});
            skCircle(sketch, "E2.14.20.0", {"center": v(13.97, -21.59) * mm, "radius": 0.5 * mm});
            skCircle(sketch, "E2.14.21.0", {"center": v(13.97, -24.13) * mm, "radius": 0.5 * mm});
            skCircle(sketch, "E2.14.22.0", {"center": v(13.97, -26.67) * mm, "radius": 0.5 * mm});
            skCircle(sketch, "E2.14.23.0", {"center": v(13.97, -29.2) * mm, "radius": 0.5 * mm});
            skCircle(sketch, "E2.15.0.0", {"center": v(16.51, 29.21) * mm, "radius": 0.5 * mm});
            skCircle(sketch, "E2.15.1.0", {"center": v(16.51, 26.67) * mm, "radius": 0.5 * mm});
            skCircle(sketch, "E2.15.2.0", {"center": v(16.51, 24.13) * mm, "radius": 0.5 * mm});
            skCircle(sketch, "E2.15.3.0", {"center": v(16.51, 21.6) * mm, "radius": 0.5 * mm});
            skCircle(sketch, "E2.15.4.0", {"center": v(16.51, 19.05) * mm, "radius": 0.5 * mm});
            skCircle(sketch, "E2.15.5.0", {"center": v(16.51, 16.51) * mm, "radius": 0.5 * mm});
            skCircle(sketch, "E2.15.6.0", {"center": v(16.51, 13.97) * mm, "radius": 0.5 * mm});
            skCircle(sketch, "E2.15.7.0", {"center": v(16.51, 11.43) * mm, "radius": 0.5 * mm});
            skCircle(sketch, "E2.15.8.0", {"center": v(16.51, 8.9) * mm, "radius": 0.5 * mm});
            skCircle(sketch, "E2.15.9.0", {"center": v(16.51, 6.35) * mm, "radius": 0.5 * mm});
            skCircle(sketch, "E2.15.10.0", {"center": v(16.51, 3.81) * mm, "radius": 0.5 * mm});
            skCircle(sketch, "E2.15.11.0", {"center": v(16.51, 1.27) * mm, "radius": 0.5 * mm});
            skCircle(sketch, "E2.15.12.0", {"center": v(16.51, -1.27) * mm, "radius": 0.5 * mm});
            skCircle(sketch, "E2.15.13.0", {"center": v(16.51, -3.8) * mm, "radius": 0.5 * mm});
            skCircle(sketch, "E2.15.14.0", {"center": v(16.51, -6.35) * mm, "radius": 0.5 * mm});
            skCircle(sketch, "E2.15.15.0", {"center": v(16.51, -8.89) * mm, "radius": 0.5 * mm});
            skCircle(sketch, "E2.15.16.0", {"center": v(16.51, -11.43) * mm, "radius": 0.5 * mm});
            skCircle(sketch, "E2.15.17.0", {"center": v(16.51, -13.97) * mm, "radius": 0.5 * mm});
            skCircle(sketch, "E2.15.18.0", {"center": v(16.51, -16.5) * mm, "radius": 0.5 * mm});
            skCircle(sketch, "E2.15.19.0", {"center": v(16.51, -19.05) * mm, "radius": 0.5 * mm});
            skCircle(sketch, "E2.15.20.0", {"center": v(16.51, -21.59) * mm, "radius": 0.5 * mm});
            skCircle(sketch, "E2.15.21.0", {"center": v(16.51, -24.13) * mm, "radius": 0.5 * mm});
            skCircle(sketch, "E2.15.22.0", {"center": v(16.51, -26.67) * mm, "radius": 0.5 * mm});
            skCircle(sketch, "E2.15.23.0", {"center": v(16.51, -29.2) * mm, "radius": 0.5 * mm});
            skCircle(sketch, "E2.16.0.0", {"center": v(19.05, 29.21) * mm, "radius": 0.5 * mm});
            skCircle(sketch, "E2.16.1.0", {"center": v(19.05, 26.67) * mm, "radius": 0.5 * mm});
            skCircle(sketch, "E2.16.2.0", {"center": v(19.05, 24.13) * mm, "radius": 0.5 * mm});
            skCircle(sketch, "E2.16.3.0", {"center": v(19.05, 21.6) * mm, "radius": 0.5 * mm});
            skCircle(sketch, "E2.16.4.0", {"center": v(19.05, 19.05) * mm, "radius": 0.5 * mm});
            skCircle(sketch, "E2.16.5.0", {"center": v(19.05, 16.51) * mm, "radius": 0.5 * mm});
            skCircle(sketch, "E2.16.6.0", {"center": v(19.05, 13.97) * mm, "radius": 0.5 * mm});
            skCircle(sketch, "E2.16.7.0", {"center": v(19.05, 11.43) * mm, "radius": 0.5 * mm});
            skCircle(sketch, "E2.16.8.0", {"center": v(19.05, 8.9) * mm, "radius": 0.5 * mm});
            skCircle(sketch, "E2.16.9.0", {"center": v(19.05, 6.35) * mm, "radius": 0.5 * mm});
            skCircle(sketch, "E2.16.10.0", {"center": v(19.05, 3.81) * mm, "radius": 0.5 * mm});
            skCircle(sketch, "E2.16.11.0", {"center": v(19.05, 1.27) * mm, "radius": 0.5 * mm});
            skCircle(sketch, "E2.16.12.0", {"center": v(19.05, -1.27) * mm, "radius": 0.5 * mm});
            skCircle(sketch, "E2.16.13.0", {"center": v(19.05, -3.8) * mm, "radius": 0.5 * mm});
            skCircle(sketch, "E2.16.14.0", {"center": v(19.05, -6.35) * mm, "radius": 0.5 * mm});
            skCircle(sketch, "E2.16.15.0", {"center": v(19.05, -8.89) * mm, "radius": 0.5 * mm});
            skCircle(sketch, "E2.16.16.0", {"center": v(19.05, -11.43) * mm, "radius": 0.5 * mm});
            skCircle(sketch, "E2.16.17.0", {"center": v(19.05, -13.97) * mm, "radius": 0.5 * mm});
            skCircle(sketch, "E2.16.18.0", {"center": v(19.05, -16.5) * mm, "radius": 0.5 * mm});
            skCircle(sketch, "E2.16.19.0", {"center": v(19.05, -19.05) * mm, "radius": 0.5 * mm});
            skCircle(sketch, "E2.16.20.0", {"center": v(19.05, -21.59) * mm, "radius": 0.5 * mm});
            skCircle(sketch, "E2.16.21.0", {"center": v(19.05, -24.13) * mm, "radius": 0.5 * mm});
            skCircle(sketch, "E2.16.22.0", {"center": v(19.05, -26.67) * mm, "radius": 0.5 * mm});
            skCircle(sketch, "E2.16.23.0", {"center": v(19.05, -29.2) * mm, "radius": 0.5 * mm});
            skCircle(sketch, "E2.17.0.0", {"center": v(21.6, 29.21) * mm, "radius": 0.5 * mm});
            skCircle(sketch, "E2.17.1.0", {"center": v(21.6, 26.67) * mm, "radius": 0.5 * mm});
            skCircle(sketch, "E2.17.2.0", {"center": v(21.6, 24.13) * mm, "radius": 0.5 * mm});
            skCircle(sketch, "E2.17.3.0", {"center": v(21.6, 21.6) * mm, "radius": 0.5 * mm});
            skCircle(sketch, "E2.17.4.0", {"center": v(21.6, 19.05) * mm, "radius": 0.5 * mm});
            skCircle(sketch, "E2.17.5.0", {"center": v(21.6, 16.51) * mm, "radius": 0.5 * mm});
            skCircle(sketch, "E2.17.6.0", {"center": v(21.6, 13.97) * mm, "radius": 0.5 * mm});
            skCircle(sketch, "E2.17.7.0", {"center": v(21.6, 11.43) * mm, "radius": 0.5 * mm});
            skCircle(sketch, "E2.17.8.0", {"center": v(21.6, 8.9) * mm, "radius": 0.5 * mm});
            skCircle(sketch, "E2.17.9.0", {"center": v(21.6, 6.35) * mm, "radius": 0.5 * mm});
            skCircle(sketch, "E2.17.10.0", {"center": v(21.6, 3.81) * mm, "radius": 0.5 * mm});
            skCircle(sketch, "E2.17.11.0", {"center": v(21.6, 1.27) * mm, "radius": 0.5 * mm});
            skCircle(sketch, "E2.17.12.0", {"center": v(21.6, -1.27) * mm, "radius": 0.5 * mm});
            skCircle(sketch, "E2.17.13.0", {"center": v(21.6, -3.8) * mm, "radius": 0.5 * mm});
            skCircle(sketch, "E2.17.14.0", {"center": v(21.6, -6.35) * mm, "radius": 0.5 * mm});
            skCircle(sketch, "E2.17.15.0", {"center": v(21.6, -8.89) * mm, "radius": 0.5 * mm});
            skCircle(sketch, "E2.17.16.0", {"center": v(21.6, -11.43) * mm, "radius": 0.5 * mm});
            skCircle(sketch, "E2.17.17.0", {"center": v(21.6, -13.97) * mm, "radius": 0.5 * mm});
            skCircle(sketch, "E2.17.18.0", {"center": v(21.6, -16.5) * mm, "radius": 0.5 * mm});
            skCircle(sketch, "E2.17.19.0", {"center": v(21.6, -19.05) * mm, "radius": 0.5 * mm});
            skCircle(sketch, "E2.17.20.0", {"center": v(21.6, -21.59) * mm, "radius": 0.5 * mm});
            skCircle(sketch, "E2.17.21.0", {"center": v(21.6, -24.13) * mm, "radius": 0.5 * mm});
            skCircle(sketch, "E2.17.22.0", {"center": v(21.6, -26.67) * mm, "radius": 0.5 * mm});
            skCircle(sketch, "E2.17.23.0", {"center": v(21.6, -29.2) * mm, "radius": 0.5 * mm});
            skLineSegment(sketch, "E2.direction1", {"start": v(-21.59, 29.21) * mm, "end": v(-19.05, 29.21) * mm, "construction": true});
            skLineSegment(sketch, "E2.direction2", {"start": v(-21.59, 29.21) * mm, "end": v(-21.59, 26.67) * mm, "construction": true});
            skSolve(sketch);
        }
        {
            var Q0;
            Q0=qSketchRegion(id+"F2",true);
            extrude(context, id + "F3", {"entities" : qUnion([Q0]), "operationType" : NewBodyOperationType.REMOVE, "endBound" : BoundingType.UP_TO_NEXT, "oppositeDirection" : true, "depth" : 25 * mm, "offsetDistance" : 25 * mm});
        }
        {
            var Q0;
            Q0=makeQuery(id+"F1.opExtrude","CAP_FACE",FACE,{"disambiguationData":[OSD([sQuery(id+"F0.wireOp",EDGE,"E0.bottom"),sQuery(id+"F0.wireOp",EDGE,"E0.top"),sQuery(id+"F0.wireOp",EDGE,"E0.left"),sQuery(id+"F0.wireOp",EDGE,"E0.right")])],"isStart":false});
            var sketch = newSketch(context, id + "F4", { "sketchPlane" : qUnion([Q0])});
            skCircle(sketch, "E3", {"center": v(-21.82, 31.83) * mm, "radius": 1.59 * mm});
            skCircle(sketch, "E4.MirrorC", {"center": v(21.82, 31.83) * mm, "radius": 1.59 * mm});
            skCircle(sketch, "E5.MirrorC", {"center": v(-21.82, -31.83) * mm, "radius": 1.59 * mm});
            skCircle(sketch, "E6.MirrorC", {"center": v(21.82, -31.83) * mm, "radius": 1.59 * mm});
            skSolve(sketch);
        }
        {
            var Q0;
            Q0=qSketchRegion(id+"F4",true);
            extrude(context, id + "F5", {"entities" : qUnion([Q0]), "operationType" : NewBodyOperationType.REMOVE, "endBound" : BoundingType.UP_TO_NEXT, "oppositeDirection" : true, "depth" : 25 * mm, "offsetDistance" : 25 * mm});
        }
    });
